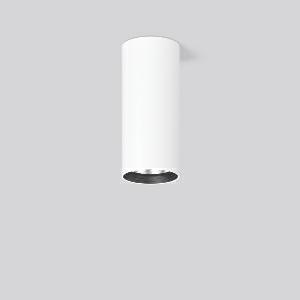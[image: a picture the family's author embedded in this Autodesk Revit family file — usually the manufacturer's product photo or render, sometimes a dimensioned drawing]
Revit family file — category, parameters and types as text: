
# Revit family: heledon_mini_a_931208_002_1_389b
name_source: partatom
category: Lighting Fixtures
units: mm (PartAtom-declared; Revit-internal decimal feet)

## family parameters
Cut with Voids When Loaded = No
Host = Face
Light Source = No
Part Type = Normal
Room Calculation Point = No
Round Connector Dimension = Use Diameter
Shared = No

## types (1)
- HELEDON mini A (1 x LED Modul 940, 3800 lm, 4000)
    Apparent Load = 29 VA
    Approval mark = CE
    CIE Flux Codes = 100 100 100 100 100
    Color Rendering = 92
    Color Temperature = 4000
    Default Elevation = 1800 mm
    Description = Series: HELEDON mini
Cylindrical surface-mounted downlight. Housing: die-cast aluminium, powder-coated. Internal ceiling frame polycarbonate with bayonet mounting. Black plastic ring and recessed LED to prevent glare from the side. Optical assembly with reflector made of MIRO-Silver with 98% total light reflection for outstanding efficiency - can be changed without tools. Best colour rendering index Ra>90. Suitable for Ceiling mounting. Easy installation with a separate ceiling frame with bayonet mounting and plug connection. Driver integrated. Connected via plug-in connector. High quality converter without flickering and stroboscopic effect. The following accessories can be mounted without use of tools: interchangeable lenses, decorative glasses, honeycomb louvre, clear and frosted diffusers, white interchangeable plastic ring. 
Colour: traffic white, matt (RAL 9016)
Diameter: 87 mm
Height: 197 mm
Lamp: LED
Socket: without socket
Colour temperature: 4000K
Colour rendering index (CRI): 92
System power: 29 W
Rated luminous flux: 3800 lm
Luminous efficiency: 131 lm/W
Control gear: Regulated power supply
Protection class: I
Type of protection: IP 20
    Height = 197 mm
    Lamp = 1 x LED Modul 940
    Lamp Light Flux = 3800 lm
    Lamp count = 1
    Length = 87 mm
    Lifetime = 50000 h
    Luminous efficacy = 131 lm/W
    Manufacturer = RZB
    ModVariant = No
    Model = 931208.002.1
    Mounting Place = Ceiling
    Mounting Type = Surface mounted
    Number of Poles = 1
    OnlyDefault = Yes
    Power Factor = 1
    Product Name = HELEDON mini A
    Product group = Surface mounted downlights
    ProductGroupID = 302
    Protection Class = Protection class I
    Protection Degree = IP 20
    RLX_Detail_Level = 1
    RLX_Emergency_Light_Flux = 0 lm
    RLX_Emergency_Type = 0
    RLX_Emergency_Type_DB = No
    RlxData = <blob elided: 106701 chars, md5=9fb4cd22>
    Socket = socket
    Standby Power = 0 W
    System Light Flux = 3800 lm
    System Power = 29 W
    Type Comments = Product without accessories
    Type Image = 931188.002.jpg
    URL = http://relux.com
    VarID = ---
    Voltage = 230 V
    Voltage Range = 220-240 V
    Weight = 0.00 kg
    Width = 0 mm  [stored 0 ft]

note: [stored X ft] marks values corroborated as IEEE doubles in the binary element streams (Revit-internal decimal feet)

## geometry (parser evidence)
native form markers: Blend x4, Sweep x10
no freeform markers — native parametric forms only
